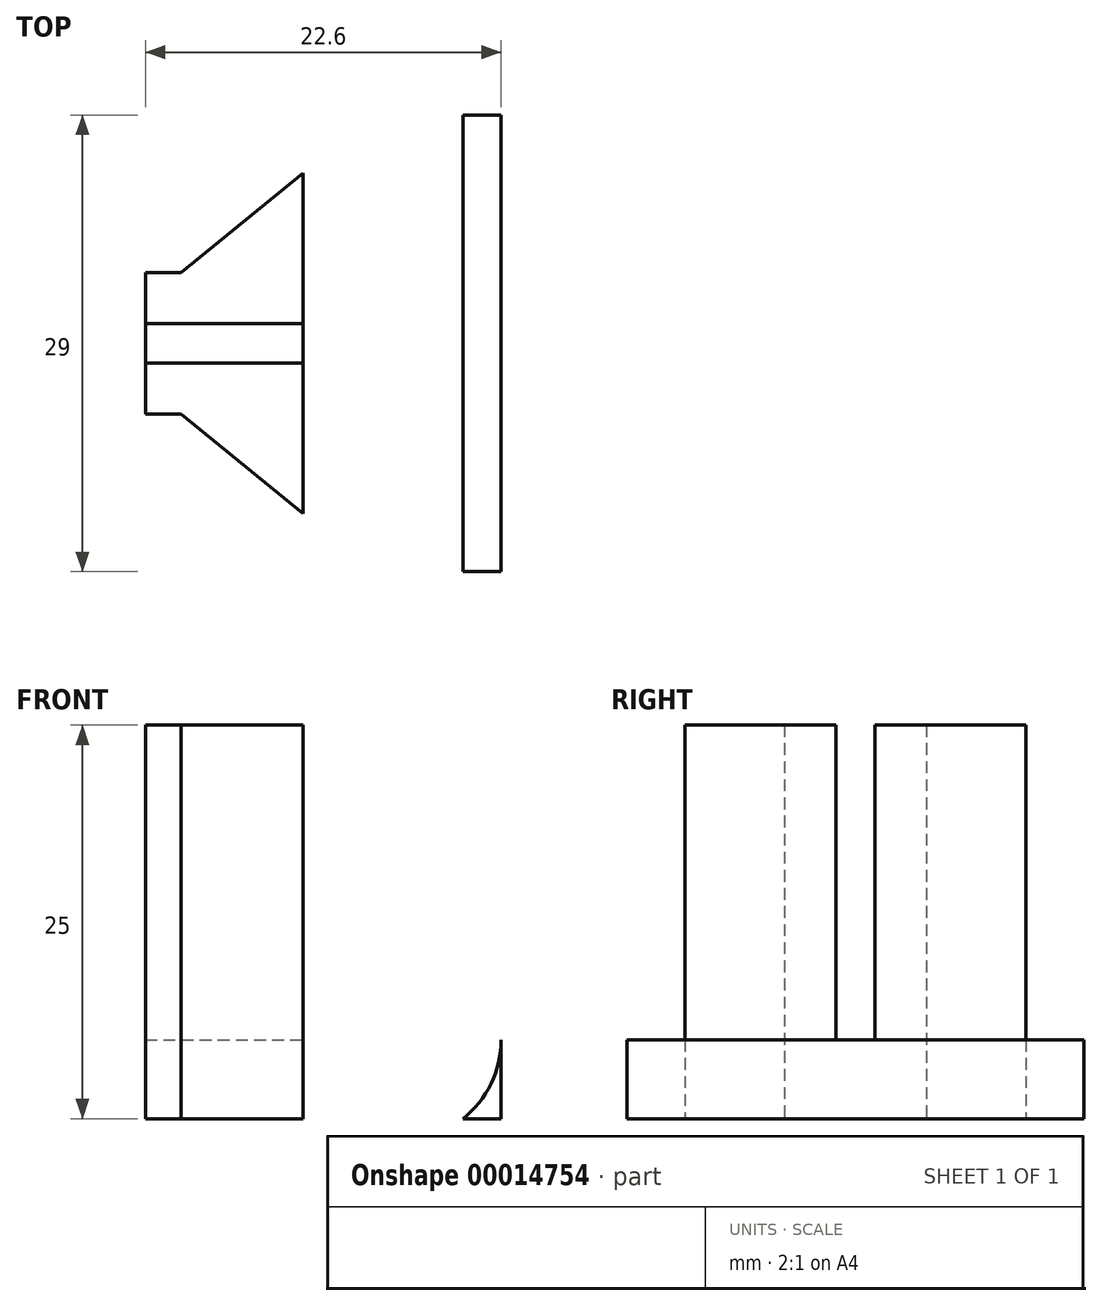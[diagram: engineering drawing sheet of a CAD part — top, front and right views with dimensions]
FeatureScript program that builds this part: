
annotation { "Feature Type Name" : "Feature", "Feature Type Description" : "" }
export const myFeature = defineFeature(function(context is Context, id is Id, definition is map)
    precondition{}
    {
        {
            var Q0;
            Q0=qCreatedBy(makeId("Top.planeOp"),FACE);
            var sketch = newSketch(context, id + "F0", { "sketchPlane" : qUnion([Q0])});
            skLineSegment(sketch, "E0", {"start": v(-14.5, -4.5) * mm, "end": v(-12.25, -4.5) * mm});
            skLineSegment(sketch, "E1", {"start": v(-4.5, -10.82) * mm, "end": v(-4.5, -14.5) * mm});
            skLineSegment(sketch, "E2", {"start": v(-4.5, -14.5) * mm, "end": v(8.1, -14.5) * mm});
            skLineSegment(sketch, "E3", {"start": v(8.1, -14.5) * mm, "end": v(8.1, 14.5) * mm});
            skLineSegment(sketch, "E4", {"start": v(8.1, 14.5) * mm, "end": v(-4.5, 14.5) * mm});
            skLineSegment(sketch, "E5", {"start": v(-4.5, 14.5) * mm, "end": v(-4.5, 10.82) * mm});
            skLineSegment(sketch, "E6", {"start": v(-12.25, 4.5) * mm, "end": v(-14.5, 4.5) * mm});
            skLineSegment(sketch, "E7", {"start": v(-14.5, 4.5) * mm, "end": v(-14.5, -4.5) * mm});
            skLineSegment(sketch, "E8", {"start": v(-12.25, -4.5) * mm, "end": v(-4.5, -10.82) * mm});
            skLineSegment(sketch, "E9", {"start": v(-12.25, 4.5) * mm, "end": v(-4.5, 10.82) * mm});
            skPoint(sketch, "E10.orphan", {"position": v(-4.5, -4.5) * mm});
            skSolve(sketch);
        }
        {
            var Q0;
            Q0=makeQuery(id+"F0.imprint","IMPRINT",FACE,{"disambiguationData":[TD([[makeQuery(id+"F0.imprint","IMPRINT",EDGE,{"derivedFrom":sQuery(id+"F0.wireOp",EDGE,"E0")}),1.0]])]});
            extrude(context, id + "F1", {"entities" : qUnion([Q0]), "depth" : 25 * mm});
        }
        {
            var Q0;
            Q0=makeQuery(id+"F1.opExtrude","CAP_FACE",FACE,{"disambiguationData":[OSD([sQuery(id+"F0.wireOp",EDGE,"E0"),sQuery(id+"F0.wireOp",EDGE,"E1"),sQuery(id+"F0.wireOp",EDGE,"E2"),sQuery(id+"F0.wireOp",EDGE,"E3"),sQuery(id+"F0.wireOp",EDGE,"E4"),sQuery(id+"F0.wireOp",EDGE,"E5"),sQuery(id+"F0.wireOp",EDGE,"E6"),sQuery(id+"F0.wireOp",EDGE,"E7")])],"isStart":false});
            var sketch = newSketch(context, id + "F2", { "sketchPlane" : qUnion([Q0])});
            skLineSegment(sketch, "E11", {"start": v(-14.5, -1.25) * mm, "end": v(-14.5, 1.25) * mm});
            skLineSegment(sketch, "E12", {"start": v(-14.5, 1.25) * mm, "end": v(-1.75, 1.25) * mm});
            skLineSegment(sketch, "E13", {"start": v(-1.75, 1.25) * mm, "end": v(-1.75, 14.5) * mm});
            skLineSegment(sketch, "E14", {"start": v(-1.75, 14.5) * mm, "end": v(1.75, 14.5) * mm});
            skLineSegment(sketch, "E15", {"start": v(1.75, 14.5) * mm, "end": v(1.75, -14.5) * mm});
            skPoint(sketch, "E15.endSnap0", {"position": v(1.8, -14.5) * mm});
            skLineSegment(sketch, "E16", {"start": v(1.75, -14.5) * mm, "end": v(-1.75, -14.5) * mm});
            skLineSegment(sketch, "E17", {"start": v(-1.75, -14.5) * mm, "end": v(-1.75, -1.25) * mm});
            skLineSegment(sketch, "E18", {"start": v(-1.75, -1.25) * mm, "end": v(-14.5, -1.25) * mm});
            skSolve(sketch);
        }
        {
            var Q0;
            Q0=makeQuery(id+"F2.imprint","IMPRINT",FACE,{"disambiguationData":[TD([[makeQuery(id+"F2.imprint","IMPRINT",EDGE,{"derivedFrom":sQuery(id+"F2.wireOp",EDGE,"E11")}),1.0]])]});
            extrude(context, id + "F3", {"entities" : qUnion([Q0]), "operationType" : NewBodyOperationType.REMOVE, "oppositeDirection" : true, "depth" : 20 * mm});
        }
        {
            var Q0;
            Q0=makeQuery(id+"F1.opExtrude","SWEPT_FACE",FACE,{"disambiguationData":[OSD([sQuery(id+"F0.wireOp",EDGE,"E2")])]});
            var sketch = newSketch(context, id + "F4", { "sketchPlane" : qUnion([Q0])});
            skLineSegment(sketch, "E19", {"start": v(1.75, 5) * mm, "end": v(8.1, 5) * mm, "construction": true});
            skLineSegment(sketch, "E20", {"start": v(8.1, 5) * mm, "end": v(1.75, 25) * mm, "construction": true});
            skArc(sketch, "E21", {"start": v(8.1, 5) * mm, "mid": v(7.46, 2.22) * mm, "end": v(5.66, 0) * mm});
            skArc(sketch, "E22", {"start": v(8.1, 5) * mm, "mid": v(8.04, 5.86) * mm, "end": v(7.87, 6.71) * mm});
            skLineSegment(sketch, "E23", {"start": v(1.75, 25) * mm, "end": v(2.75, 25) * mm});
            skLineSegment(sketch, "E24", {"start": v(2.75, 25) * mm, "end": v(7.87, 6.71) * mm});
            skSolve(sketch);
        }
        {
            var Q0;
            {var subQ0=sQuery(id+"F4.wireOp",EDGE,"E22");Q0=makeQuery(id+"F4.imprint","IMPRINT",FACE,{"disambiguationData":[TD([[makeQuery(id+"F4.imprint","IMPRINT",EDGE,{"derivedFrom":subQ0}),-1.0]])]});}
            extrude(context, id + "F5", {"entities" : qUnion([Q0]), "operationType" : NewBodyOperationType.REMOVE, "endBound" : BoundingType.THROUGH_ALL, "oppositeDirection" : true, "depth" : 25 * mm});
        }
        {
            var Q0;
            {var subQ0=sQuery(id+"F4.wireOp",EDGE,"E21");Q0=makeQuery(id+"F4.imprint","IMPRINT",FACE,{"disambiguationData":[TD([[makeQuery(id+"F4.imprint","IMPRINT",EDGE,{"derivedFrom":subQ0}),1.0]])]});}
            extrude(context, id + "F6", {"entities" : qUnion([Q0]), "operationType" : NewBodyOperationType.REMOVE, "endBound" : BoundingType.THROUGH_ALL, "oppositeDirection" : true, "depth" : 25 * mm});
        }
    });
